# Revit family: Шкаф металлический формата А1 на 5-15 ящиков
name_source: partatom
category: Оборудование
revit_build: Autodesk Revit 2017 (Build: 20170419_0315(x64)
units: mm (PartAtom-declared; Revit-internal decimal feet)

## family parameters
Всегда вертикально = Да
На основе рабочей плоскости = Нет
Общий = Нет
При загрузке вырезать с полостями = Нет
Размер круглого соединителя = Использовать диаметр
Тип детали = Нормальный
Точка расчета площади = Нет

## types (2) — shared parameters
Единицы = шт.
Код оборудования = -
Ширина = 1010 мм
шш = 970 мм

## per-type parameters (varying)
| type | Высота | Глубина | Группа модели | Завод | Изготовитель | Масса | Материал | Наименование | Обозначение | вв | кол-во ящиков |
| 10 ящиков | 835 мм | 915 мм | ТХ | Торговая сеть | Ant | 134 | ЛДСП | Шкаф металлический для хранения документов формата А1, 10 ящиков | Комплект в составе: A1-05/3 (нижняя секция), A1-05/0 (верхняя секция), разделители для формата А2 (10 шт.) | 68.5 мм | 10 |
| 15 ящиков | 1300 мм | 691 мм |  | Практик | Severin | 194 | Металл окрашенный серый | Шкаф металлический для хранения документов формата А1, 15 ящиков | Комплект в составе: A1-05/3 (нижняя секция), A1-05/2 (центральная секция), A1-05/0 (верхняя секция), разделители для формата А2, (15 шт.) | 66.5 мм | 15 |

## geometry (parser evidence)
native form markers: Blend x2
no freeform markers — native parametric forms only
